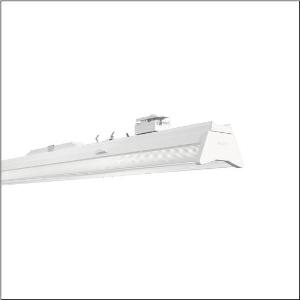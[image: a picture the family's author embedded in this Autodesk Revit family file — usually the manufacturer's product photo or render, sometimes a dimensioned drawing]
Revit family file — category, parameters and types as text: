
# Revit family: licross_r__21_performance_mo_52td16dn445g_3218
name_source: partatom
category: Lighting Fixtures
units: mm (PartAtom-declared; Revit-internal decimal feet)

## family parameters
Cut with Voids When Loaded = No
Host = Face
Light Source = No
Part Type = Normal
Room Calculation Point = No
Round Connector Dimension = Use Diameter
Shared = No

## types (1)
- --- (1 x LED, 4500 lm, 24.9 W, 4000K)
    Apparent Load = 25 VA
    CIE Flux Codes = 66 88 96 79 100
    Color Rendering = 80
    Color Temperature = 4000K
    Default Elevation = 1800 mm
    Description = Licross® 21 Performance MO, luminaire insert, of sheet steel, galvanised, coil coated, white, length: 1.500mm, width: 120mm, height: 123mm, LED rated luminous flux: 4.500lm, light colour: 840, control gear: DALI 2, with plug, 5-pole, with phase selection, mains connection: 220..240V, AC, 50/60Hz, rated input power: 25W, halogen-free wiring, primary light control with lens, of plastic, primary optical cover: cover, of PMMA, CAT 2 (L<= 3000cd/m²), light emission: direct/indirect distribution, primary light characteristic: symmetric, protection rating (complete): IP54, insulation class (complete): insulation class I (protective earthing), certification: CE, ENEC, VDE, UKCA, protection symbol: D if used in an environment with non-conductive dust loads with corresponding accessories, impact resistance: IK06, permissible ambient temperature for indoor applications: -25..+50°C, corresponds to IFS (International Featured Standards) requirements for safety and quality in the food industry, reducing of maximum allowable ambient temperature of 5°C with ceiling mounting, LABS conformity tested according to VDMA 24364:2018-05, packaging unit: 1 piece
    Height = 114 mm
    Lamp = 1 x LED
    Lamp Light Flux = 4500 lm
    Lamp Power = 24.9 W
    Lamp count = 1
    Length = 1500 mm
    Luminous efficacy = 181 lm/W
    Manufacturer = Siteco
    ModVariant = No
    Model = 52TD16DN445G
    Mounting Place = Ceiling
    Mounting Type = Pendant
    Number of Poles = 1
    OnlyDefault = Yes
    Power Factor = 1
    Product Name = Licross® 21 Performance MO
    Product group = luminaire insert
    ProductGroupID = 901
    Protection Class = Protection class I
    Protection Degree = IP 54
    RLX_Detail_Level = 1
    RLX_Emergency_Light_Flux = 0 lm
    RLX_Emergency_Type = 0
    RLX_Emergency_Type_DB = No
    RlxData = <blob elided: 33513 chars, md5=948fc94e>
    Socket = socket
    Standby Power = 0 W
    System Light Flux = 4500 lm
    System Power = 25 W
    Type Comments = factory setting: luminous flux: 100 % | dim-lin: 254 | 165 mA
    Type Image = l_1256138.jpg
    URL = http://relux.com
    VarID = @adj_000101
    Voltage = 0 V
    Weight = 0.00 kg
    Width = 120 mm

## geometry (parser evidence)
native form markers: Blend x4, Sweep x11
no freeform markers — native parametric forms only
